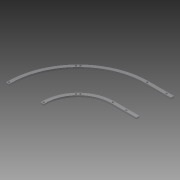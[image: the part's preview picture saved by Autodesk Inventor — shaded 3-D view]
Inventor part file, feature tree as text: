
AUTODESK INVENTOR PART (.ipt)
format: ipt  version: 2013 (Build 170138000, 138)  size: 118,784 bytes
history: native  units: in
note: dims shown in document units (in); Inventor stores cm internally (conversion verified against a paired STEP export)
features: extrude x1, sketch x1
ambient origin geometry x8: Origin, YZ Plane, XZ Plane, XY Plane, X Axis, Y Axis, Z Axis, Center Point
bodies: Solid1 (feature_tree)
feature tree (2):
  extrude  "Extrusion1"  Depth=0.25in TaperAngle=0.0deg
  sketch  "Sketch1"  dims[d2=0.5in d3=0.5in d10=0.5in d11=0.5in d13=0.5in d14=0.266in d15=0.266in d16=0.266in d18=0.266in d20=0.25in d21=0.266in d22=0.266in d23=0.266in d24=0.25in d26=0.266in d27=0.25in d30=0.266in d31=0.25in d32=0.266in d33=0.25in d34=0.25in d35=0.0in]
